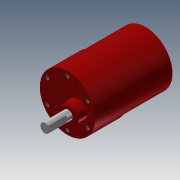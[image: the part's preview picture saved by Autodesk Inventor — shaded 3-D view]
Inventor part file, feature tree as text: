
AUTODESK INVENTOR PART (.ipt)
format: ipt  version: 2013 (Build 170138000, 138)  size: 151,552 bytes
history: native  units: mm
features: sketch x9, extrude x6, fillet x1, chamfer x1, hole x1
ambient origin geometry x8: Origin, YZ Plane, XZ Plane, XY Plane, X Axis, Y Axis, Z Axis, Center Point
bodies: Solid1 (feature_tree)
feature tree (18):
  extrude  "Extrusion1"  Depth=22.0mm TaperAngle=0.0deg
  extrude  "Extrusion2"  Depth=30.0mm TaperAngle=0.0deg
  fillet  "Fillet1"  Radius=0.5mm
  extrude  "Extrusion3"  Depth=12.0mm
  extrude  "Extrusion4"  Depth=6.0mm
  extrude  "Extrusion5"  Depth=12.0mm TaperAngle=0.0deg
  chamfer  "Chamfer1"  Distance=1.0mm Angle=45.0deg
  extrude  "Extrusion6"  Depth=12.0mm TaperAngle=0.0deg
  hole  "Hole1"  [1 undecoded]
  sketch  "Sketch8"  dims[d24=2.4mm]
  sketch  "Sketch9"  dims[d28=2.4mm d29=2.4mm d32=2.4mm d33=15.5mm d34=2.4mm d35=2.459mm d36=3.0mm d37=4.0mm d38=2.0mm d39=90.0deg d40=3.0mm d41=0.0mm]
  sketch  "Sketch1"  dims[d0=36.8mm d1=22.0mm d2=0.0mm]
  sketch  "Sketch2"  dims[d3=35.8mm d4=30.0mm d5=0.0mm d6=0.5mm]
  sketch  "Sketch3"  dims[d7=7.0mm d8=12.0mm]
  sketch  "Sketch4"  dims[d9=6.5mm d10=0.0mm d11=6.0mm]
  sketch  "Sketch5"  dims[d12=3.5mm d13=0.0mm d14=12.0mm d15=0.0mm d16=1.0mm d17=2.0mm d18=45.0deg]
  sketch  "Sketch6"  dims[d19=0.6mm d20=12.0mm d21=0.0mm]
  sketch  "Sketch7"  dims[d22=31.0mm d23=2.4mm]
note: 1 required parameter value undecoded (feature->parameter linkage not recoverable at this tier; creation-order binding heuristic only, values carry confidence <= 0.55)
